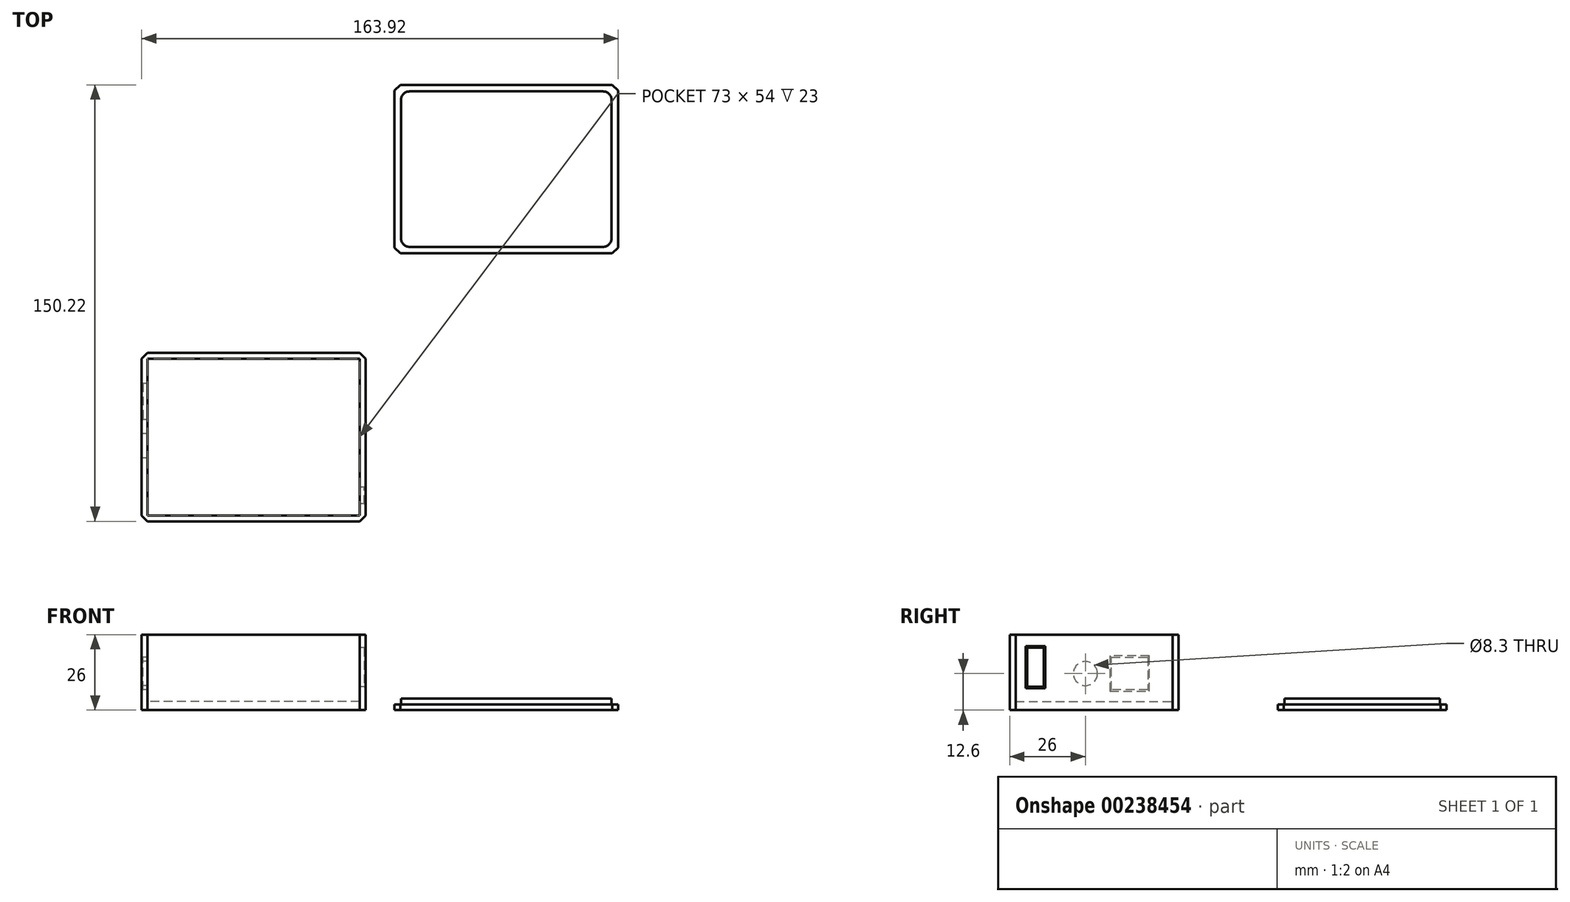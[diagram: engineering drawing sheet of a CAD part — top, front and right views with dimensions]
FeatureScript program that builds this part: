
annotation { "Feature Type Name" : "Feature", "Feature Type Description" : "" }
export const myFeature = defineFeature(function(context is Context, id is Id, definition is map)
    precondition{}
    {
        {
            var Q0;
            Q0=qCreatedBy(makeId("Top.planeOp"),FACE);
            var sketch = newSketch(context, id + "F0", { "sketchPlane" : qUnion([Q0])});
            skLineSegment(sketch, "E0.bottom", {"start": v(38.5, -29) * mm, "end": v(-38.5, -29) * mm});
            skLineSegment(sketch, "E0.top", {"start": v(38.5, 29) * mm, "end": v(-38.5, 29) * mm});
            skLineSegment(sketch, "E0.left", {"start": v(38.5, -29) * mm, "end": v(38.5, 29) * mm});
            skLineSegment(sketch, "E0.right", {"start": v(-38.5, -29) * mm, "end": v(-38.5, 29) * mm});
            skPoint(sketch, "E0.middle", {"position": v(0, 0) * mm});
            skSolve(sketch);
        }
        {
            var Q0;
            Q0 = qSketchRegion(id + "F0", true);
            extrude(context, id + "F1", {"entities" : qUnion([Q0]), "depth" : 3 * mm});
        }
        {
            var Q0;
            Q0=makeQuery(id+"F1.opExtrude","CAP_FACE",FACE,{"disambiguationData":[OSD([sQuery(id+"F0.wireOp",EDGE,"E0.bottom"),sQuery(id+"F0.wireOp",EDGE,"E0.top"),sQuery(id+"F0.wireOp",EDGE,"E0.left"),sQuery(id+"F0.wireOp",EDGE,"E0.right")])],"isStart":false});
            var sketch = newSketch(context, id + "F2", { "sketchPlane" : qUnion([Q0])});
            skLineSegment(sketch, "E1.0", {"start": v(-36.5, -27) * mm, "end": v(-36.5, 27) * mm});
            skLineSegment(sketch, "E1.1", {"start": v(36.5, -27) * mm, "end": v(-36.5, -27) * mm});
            skLineSegment(sketch, "E1.2", {"start": v(36.5, -27) * mm, "end": v(36.5, 27) * mm});
            skLineSegment(sketch, "E1.3", {"start": v(36.5, 27) * mm, "end": v(-36.5, 27) * mm});
            skSolve(sketch);
        }
        {
            var Q0;
            Q0=makeQuery(id+"F2.imprint","IMPRINT",FACE,{"disambiguationData":[TD([[makeQuery(id+"F2.imprint","IMPRINT",EDGE,{"derivedFrom":sQuery(id+"F2.wireOp",EDGE,"E1.0")}),1.0]])]});
            extrude(context, id + "F3", {"entities" : qUnion([Q0]), "operationType" : NewBodyOperationType.ADD, "depth" : 4 * mm});
        }
        {
            var Q0;
            Q0=makeQuery(id+"F3.opExtrude","CAP_FACE",FACE,{"disambiguationData":[OSD([sQuery(id+"F0.wireOp",EDGE,"E0.bottom"),sQuery(id+"F0.wireOp",EDGE,"E0.top"),sQuery(id+"F0.wireOp",EDGE,"E0.left"),sQuery(id+"F0.wireOp",EDGE,"E0.right"),sQuery(id+"F2.wireOp",EDGE,"E1.0"),sQuery(id+"F2.wireOp",EDGE,"E1.1"),sQuery(id+"F2.wireOp",EDGE,"E1.2"),sQuery(id+"F2.wireOp",EDGE,"E1.3")])],"isStart":false});
            var sketch = newSketch(context, id + "F4", { "sketchPlane" : qUnion([Q0])});
            skLineSegment(sketch, "E2", {"start": v(-36.5, 27) * mm, "end": v(-36.5, 18.5) * mm, "construction": true});
            skLineSegment(sketch, "E3", {"start": v(-36.5, 18.5) * mm, "end": v(-38.5, 18.5) * mm});
            skLineSegment(sketch, "E4", {"start": v(-36.5, 6) * mm, "end": v(-38.5, 6) * mm});
            skSolve(sketch);
        }
        {
            var Q0;
            {var subQ2=sQuery(id+"F4.wireOp",EDGE,"E3");Q0=makeQuery(id+"F4.imprint","IMPRINT",FACE,{"disambiguationData":[TD([[makeQuery(id+"F4.imprint","IMPRINT",EDGE,{"derivedFrom":subQ2}),-1.0]])]});}
            extrude(context, id + "F5", {"entities" : qUnion([Q0]), "operationType" : NewBodyOperationType.ADD, "depth" : 19 * mm});
        }
        {
            var Q0;
            Q0=makeQuery(id+"F5.opExtrude","SWEPT_FACE",FACE,{"disambiguationData":[OSD([sQuery(id+"F4.wireOp",EDGE,"E3")])]});
            var sketch = newSketch(context, id + "F6", { "sketchPlane" : qUnion([Q0])});
            skLineSegment(sketch, "E5", {"start": v(-38.5, 18.2) * mm, "end": v(-36.5, 18.2) * mm});
            skSolve(sketch);
        }
        {
            var Q0;
            Q0 = qSketchRegion(id + "F6", true);
            var Q1;
            {var subQ0=sQuery(id+"F6.wireOp",EDGE,"E5");Q1=makeQuery(id+"F6.imprint","IMPRINT",FACE,{"disambiguationData":[TD([[makeQuery(id+"F6.imprint","IMPRINT",EDGE,{"derivedFrom":subQ0}),1.0]])]});}
            extrude(context, id + "F7", {"entities" : qUnion([Q0, Q1]), "operationType" : NewBodyOperationType.ADD, "depth" : 25 * mm});
        }
        {
            var Q0;
            {var subQ0=sQuery(id+"F4.wireOp",EDGE,"E3");var subQ1=sQuery(id+"F0.wireOp",EDGE,"E0.right");var subQ2=makeQuery(id+"F3.opExtrude","CAP_EDGE",EDGE,{"disambiguationData":[OSD([subQ1])],"isStart":false});Q0=makeQuery(id+"F7.boolean.opBoolean","MERGE",FACE,{"derivedFrom":[makeQuery(id+"F5.boolean.opBoolean","MERGE",FACE,{"derivedFrom":[makeQuery(id+"F3.boolean.opBoolean","MERGE",FACE,{"derivedFrom":[makeQuery(id+"F1.opExtrude","SWEPT_FACE",FACE,{"disambiguationData":[OSD([subQ1])]}),makeQuery(id+"F3.opExtrude","SWEPT_FACE",FACE,{"disambiguationData":[OSD([subQ1])]})]}),makeQuery(id+"F5.opExtrude","SWEPT_FACE",FACE,{"disambiguationData":[OSD([subQ1]),TDD([makeQuery(id+"F4.imprint","IMPRINT",EDGE,{"disambiguationData":[TD([[makeQuery(id+"F4.imprint","INTERSECT",VERTEX,{"derivedFrom":[makeQuery(id+"F3.opExtrude","CAP_EDGE",EDGE,{"disambiguationData":[OSD([sQuery(id+"F0.wireOp",EDGE,"E0.bottom")])],"isStart":false}),subQ2]}),-1.0]])],"derivedFrom":subQ2})])]}),makeQuery(id+"F5.opExtrude","SWEPT_FACE",FACE,{"disambiguationData":[OSD([subQ1]),TDD([makeQuery(id+"F4.imprint","IMPRINT",EDGE,{"disambiguationData":[TD([[makeQuery(id+"F4.imprint","INTERSECT",VERTEX,{"derivedFrom":[makeQuery(id+"F3.opExtrude","CAP_EDGE",EDGE,{"disambiguationData":[OSD([sQuery(id+"F0.wireOp",EDGE,"E0.top")])],"isStart":false}),subQ2]}),1.0]])],"derivedFrom":subQ2})])]})]}),makeQuery(id+"F7.opExtrude","SWEPT_FACE",FACE,{"disambiguationData":[OSD([subQ1,subQ0])]})]});}
            var sketch = newSketch(context, id + "F8", { "sketchPlane" : qUnion([Q0])});
            skLineSegment(sketch, "E6", {"start": v(-6, 12.6) * mm, "end": v(3, 12.6) * mm, "construction": true});
            skPoint(sketch, "E7", {"position": v(3, 12.6) * mm});
            skSolve(sketch);
        }
        {
            var Q0;
            Q0=sQuery(id+"F8.wireOp",VERTEX,"E7");
            var Q1;
            Q1=makeQuery(id+"F1.opExtrude","SWEPT_BODY",BODY,{"disambiguationData":[OSD([sQuery(id+"F0.wireOp",EDGE,"E0.bottom"),sQuery(id+"F0.wireOp",EDGE,"E0.top"),sQuery(id+"F0.wireOp",EDGE,"E0.left"),sQuery(id+"F0.wireOp",EDGE,"E0.right")])]});
            hole(context, id + "F9", {"style" : HoleStyle.SIMPLE, "endStyle" : HoleEndStyle.BLIND, "holeDiameter" : 8.3 * mm, "holeDepth" : 10 * mm, "locations" : qUnion([Q0]), "scope" : qUnion([Q1])});
        }
        {
            var Q0;
            {var subQ0=sQuery(id+"F2.wireOp",EDGE,"E1.2");Q0=makeQuery(id+"F5.boolean.opBoolean","MERGE",FACE,{"derivedFrom":[makeQuery(id+"F3.opExtrude","SWEPT_FACE",FACE,{"disambiguationData":[OSD([subQ0])]}),makeQuery(id+"F5.opExtrude","SWEPT_FACE",FACE,{"disambiguationData":[OSD([subQ0])]})]});}
            var sketch = newSketch(context, id + "F10", { "sketchPlane" : qUnion([Q0])});
            skLineSegment(sketch, "E8", {"start": v(23, 3) * mm, "end": v(23, 8) * mm, "construction": true});
            skLineSegment(sketch, "E9", {"start": v(23, 8) * mm, "end": v(27, 8) * mm});
            skLineSegment(sketch, "E10.bottom", {"start": v(23, 8) * mm, "end": v(17.3, 8) * mm});
            skLineSegment(sketch, "E10.top", {"start": v(23, 21.5) * mm, "end": v(17.3, 21.5) * mm});
            skLineSegment(sketch, "E10.left", {"start": v(23, 8) * mm, "end": v(23, 21.5) * mm});
            skLineSegment(sketch, "E10.right", {"start": v(17.3, 8) * mm, "end": v(17.3, 21.5) * mm});
            skSolve(sketch);
        }
        {
            var Q0;
            Q0 = qSketchRegion(id + "F10", true);
            extrude(context, id + "F11", {"entities" : qUnion([Q0]), "operationType" : NewBodyOperationType.REMOVE, "oppositeDirection" : true, "depth" : 25 * mm});
        }
        {
            var Q0;
            {var subQ0=sQuery(id+"F0.wireOp",EDGE,"E0.right");var subQ1=sQuery(id+"F0.wireOp",EDGE,"E0.bottom");Q0=makeQuery(id+"F5.boolean.opBoolean","MERGE",EDGE,{"derivedFrom":[makeQuery(id+"F3.boolean.opBoolean","MERGE",EDGE,{"derivedFrom":[makeQuery(id+"F1.opExtrude","SWEPT_EDGE",EDGE,{"disambiguationData":[OSD([subQ1,subQ0])]}),makeQuery(id+"F3.opExtrude","SWEPT_EDGE",EDGE,{"disambiguationData":[OSD([subQ1,subQ0])]})]}),makeQuery(id+"F5.opExtrude","SWEPT_EDGE",EDGE,{"disambiguationData":[OSD([subQ1,subQ0])]})]});}
            var Q1;
            {var subQ0=sQuery(id+"F0.wireOp",EDGE,"E0.left");var subQ1=sQuery(id+"F0.wireOp",EDGE,"E0.bottom");Q1=makeQuery(id+"F5.boolean.opBoolean","MERGE",EDGE,{"derivedFrom":[makeQuery(id+"F3.boolean.opBoolean","MERGE",EDGE,{"derivedFrom":[makeQuery(id+"F1.opExtrude","SWEPT_EDGE",EDGE,{"disambiguationData":[OSD([subQ1,subQ0])]}),makeQuery(id+"F3.opExtrude","SWEPT_EDGE",EDGE,{"disambiguationData":[OSD([subQ1,subQ0])]})]}),makeQuery(id+"F5.opExtrude","SWEPT_EDGE",EDGE,{"disambiguationData":[OSD([subQ1,subQ0])]})]});}
            var Q2;
            {var subQ0=sQuery(id+"F0.wireOp",EDGE,"E0.left");var subQ1=sQuery(id+"F0.wireOp",EDGE,"E0.top");Q2=makeQuery(id+"F5.boolean.opBoolean","MERGE",EDGE,{"derivedFrom":[makeQuery(id+"F3.boolean.opBoolean","MERGE",EDGE,{"derivedFrom":[makeQuery(id+"F1.opExtrude","SWEPT_EDGE",EDGE,{"disambiguationData":[OSD([subQ1,subQ0])]}),makeQuery(id+"F3.opExtrude","SWEPT_EDGE",EDGE,{"disambiguationData":[OSD([subQ1,subQ0])]})]}),makeQuery(id+"F5.opExtrude","SWEPT_EDGE",EDGE,{"disambiguationData":[OSD([subQ1,subQ0])]})]});}
            var Q3;
            {var subQ0=sQuery(id+"F0.wireOp",EDGE,"E0.right");var subQ1=sQuery(id+"F0.wireOp",EDGE,"E0.top");Q3=makeQuery(id+"F5.boolean.opBoolean","MERGE",EDGE,{"derivedFrom":[makeQuery(id+"F3.boolean.opBoolean","MERGE",EDGE,{"derivedFrom":[makeQuery(id+"F1.opExtrude","SWEPT_EDGE",EDGE,{"disambiguationData":[OSD([subQ1,subQ0])]}),makeQuery(id+"F3.opExtrude","SWEPT_EDGE",EDGE,{"disambiguationData":[OSD([subQ1,subQ0])]})]}),makeQuery(id+"F5.opExtrude","SWEPT_EDGE",EDGE,{"disambiguationData":[OSD([subQ1,subQ0])]})]});}
            chamfer(context, id + "F12", {"entities" : qUnion([Q0, Q1, Q2, Q3]), "width" : 2 * mm, "tangentPropagation" : true});
        }
        {
            var Q0;
            {var subQ0=sQuery(id+"F0.wireOp",EDGE,"E0.left");Q0=makeQuery(id+"F11.boolean.opBoolean","INTERSECT",EDGE,{"derivedFrom":[makeQuery(id+"F5.boolean.opBoolean","MERGE",FACE,{"derivedFrom":[makeQuery(id+"F3.boolean.opBoolean","MERGE",FACE,{"derivedFrom":[makeQuery(id+"F1.opExtrude","SWEPT_FACE",FACE,{"disambiguationData":[OSD([subQ0])]}),makeQuery(id+"F3.opExtrude","SWEPT_FACE",FACE,{"disambiguationData":[OSD([subQ0])]})]}),makeQuery(id+"F5.opExtrude","SWEPT_FACE",FACE,{"disambiguationData":[OSD([subQ0])]})]}),makeQuery(id+"F11.opExtrude","SWEPT_FACE",FACE,{"disambiguationData":[OSD([sQuery(id+"F10.wireOp",EDGE,"E10.right")])]})]});}
            var Q1;
            {var subQ0=sQuery(id+"F0.wireOp",EDGE,"E0.left");Q1=makeQuery(id+"F11.boolean.opBoolean","INTERSECT",EDGE,{"derivedFrom":[makeQuery(id+"F5.boolean.opBoolean","MERGE",FACE,{"derivedFrom":[makeQuery(id+"F3.boolean.opBoolean","MERGE",FACE,{"derivedFrom":[makeQuery(id+"F1.opExtrude","SWEPT_FACE",FACE,{"disambiguationData":[OSD([subQ0])]}),makeQuery(id+"F3.opExtrude","SWEPT_FACE",FACE,{"disambiguationData":[OSD([subQ0])]})]}),makeQuery(id+"F5.opExtrude","SWEPT_FACE",FACE,{"disambiguationData":[OSD([subQ0])]})]}),makeQuery(id+"F11.opExtrude","SWEPT_FACE",FACE,{"disambiguationData":[OSD([sQuery(id+"F10.wireOp",EDGE,"E10.top")])]})]});}
            var Q2;
            {var subQ0=sQuery(id+"F0.wireOp",EDGE,"E0.left");Q2=makeQuery(id+"F11.boolean.opBoolean","INTERSECT",EDGE,{"derivedFrom":[makeQuery(id+"F5.boolean.opBoolean","MERGE",FACE,{"derivedFrom":[makeQuery(id+"F3.boolean.opBoolean","MERGE",FACE,{"derivedFrom":[makeQuery(id+"F1.opExtrude","SWEPT_FACE",FACE,{"disambiguationData":[OSD([subQ0])]}),makeQuery(id+"F3.opExtrude","SWEPT_FACE",FACE,{"disambiguationData":[OSD([subQ0])]})]}),makeQuery(id+"F5.opExtrude","SWEPT_FACE",FACE,{"disambiguationData":[OSD([subQ0])]})]}),makeQuery(id+"F11.opExtrude","SWEPT_FACE",FACE,{"disambiguationData":[OSD([sQuery(id+"F10.wireOp",EDGE,"E10.left")])]})]});}
            var Q3;
            {var subQ0=sQuery(id+"F0.wireOp",EDGE,"E0.left");Q3=makeQuery(id+"F11.boolean.opBoolean","INTERSECT",EDGE,{"derivedFrom":[makeQuery(id+"F5.boolean.opBoolean","MERGE",FACE,{"derivedFrom":[makeQuery(id+"F3.boolean.opBoolean","MERGE",FACE,{"derivedFrom":[makeQuery(id+"F1.opExtrude","SWEPT_FACE",FACE,{"disambiguationData":[OSD([subQ0])]}),makeQuery(id+"F3.opExtrude","SWEPT_FACE",FACE,{"disambiguationData":[OSD([subQ0])]})]}),makeQuery(id+"F5.opExtrude","SWEPT_FACE",FACE,{"disambiguationData":[OSD([subQ0])]})]}),makeQuery(id+"F11.opExtrude","SWEPT_FACE",FACE,{"disambiguationData":[OSD([sQuery(id+"F10.wireOp",EDGE,"E10.bottom")])]})]});}
            chamfer(context, id + "F13", {"entities" : qUnion([Q0, Q1, Q2, Q3]), "width" : .5 * mm, "tangentPropagation" : true});
        }
        {
            var Q0;
            Q0=makeQuery(id+"F5.opExtrude","SWEPT_EDGE",EDGE,{"disambiguationData":[OSD([sQuery(id+"F0.wireOp",EDGE,"E0.right"),sQuery(id+"F4.wireOp",EDGE,"E3")])]});
            var Q1;
            Q1=makeQuery(id+"F7.opExtrude","SWEPT_EDGE",EDGE,{"disambiguationData":[OSD([sQuery(id+"F0.wireOp",EDGE,"E0.right"),sQuery(id+"F4.wireOp",EDGE,"E3"),sQuery(id+"F6.wireOp",EDGE,"E5")])]});
            var Q2;
            Q2=makeQuery(id+"F5.opExtrude","SWEPT_EDGE",EDGE,{"disambiguationData":[OSD([sQuery(id+"F0.wireOp",EDGE,"E0.right"),sQuery(id+"F4.wireOp",EDGE,"E4")])]});
            var Q3;
            Q3=makeQuery(id+"F3.opExtrude","CAP_EDGE",EDGE,{"disambiguationData":[OSD([sQuery(id+"F0.wireOp",EDGE,"E0.right")])],"isStart":false});
            chamfer(context, id + "F14", {"entities" : qUnion([Q0, Q1, Q2, Q3]), "width" : .5 * mm, "tangentPropagation" : true});
        }
        {
            var Q0;
            Q0=qCreatedBy(makeId("Top.planeOp"),FACE);
            var sketch = newSketch(context, id + "F15", { "sketchPlane" : qUnion([Q0])});
            skLineSegment(sketch, "E11.bottom", {"start": v(48.42, 63.22) * mm, "end": v(125.42, 63.22) * mm});
            skLineSegment(sketch, "E11.top", {"start": v(48.42, 121.22) * mm, "end": v(125.42, 121.22) * mm});
            skLineSegment(sketch, "E11.left", {"start": v(48.42, 63.22) * mm, "end": v(48.42, 121.22) * mm});
            skLineSegment(sketch, "E11.right", {"start": v(125.42, 63.22) * mm, "end": v(125.42, 121.22) * mm});
            skSolve(sketch);
        }
        {
            var Q0;
            Q0 = qSketchRegion(id + "F15", true);
            extrude(context, id + "F16", {"entities" : qUnion([Q0]), "depth" : 2 * mm});
        }
        {
            var Q0;
            Q0=makeQuery(id+"F16.opExtrude","CAP_FACE",FACE,{"disambiguationData":[OSD([sQuery(id+"F15.wireOp",EDGE,"E11.bottom"),sQuery(id+"F15.wireOp",EDGE,"E11.top"),sQuery(id+"F15.wireOp",EDGE,"E11.left"),sQuery(id+"F15.wireOp",EDGE,"E11.right")])],"isStart":false});
            var sketch = newSketch(context, id + "F17", { "sketchPlane" : qUnion([Q0])});
            skLineSegment(sketch, "E12.0", {"start": v(50.67, 118.97) * mm, "end": v(123.17, 118.97) * mm});
            skLineSegment(sketch, "E12.1", {"start": v(50.67, 65.47) * mm, "end": v(50.67, 118.97) * mm});
            skLineSegment(sketch, "E12.2", {"start": v(50.67, 65.47) * mm, "end": v(123.17, 65.47) * mm});
            skLineSegment(sketch, "E12.3", {"start": v(123.17, 65.47) * mm, "end": v(123.17, 118.97) * mm});
            skSolve(sketch);
        }
        {
            var Q0;
            Q0 = qSketchRegion(id + "F17", true);
            extrude(context, id + "F18", {"entities" : qUnion([Q0]), "operationType" : NewBodyOperationType.ADD, "depth" : 2 * mm});
        }
        {
            var Q0;
            Q0=makeQuery(id+"F18.opExtrude","SWEPT_EDGE",EDGE,{"disambiguationData":[OSD([sQuery(id+"F17.wireOp",EDGE,"E12.2"),sQuery(id+"F17.wireOp",EDGE,"E12.3")])]});
            var Q1;
            Q1=makeQuery(id+"F18.opExtrude","SWEPT_EDGE",EDGE,{"disambiguationData":[OSD([sQuery(id+"F17.wireOp",EDGE,"E12.1"),sQuery(id+"F17.wireOp",EDGE,"E12.2")])]});
            var Q2;
            Q2=makeQuery(id+"F18.opExtrude","SWEPT_EDGE",EDGE,{"disambiguationData":[OSD([sQuery(id+"F17.wireOp",EDGE,"E12.0"),sQuery(id+"F17.wireOp",EDGE,"E12.1")])]});
            var Q3;
            Q3=makeQuery(id+"F18.opExtrude","SWEPT_EDGE",EDGE,{"disambiguationData":[OSD([sQuery(id+"F17.wireOp",EDGE,"E12.0"),sQuery(id+"F17.wireOp",EDGE,"E12.3")])]});
            fillet(context, id + "F19", {"entities" : qUnion([Q0, Q1, Q2, Q3]), "radius" : 3 * mm, "tangentPropagation" : true, "allowEdgeOverflow" : false});
        }
        {
            var Q0;
            Q0=makeQuery(id+"F16.opExtrude","SWEPT_EDGE",EDGE,{"disambiguationData":[OSD([sQuery(id+"F15.wireOp",EDGE,"E11.top"),sQuery(id+"F15.wireOp",EDGE,"E11.left")])]});
            var Q1;
            Q1=makeQuery(id+"F16.opExtrude","SWEPT_EDGE",EDGE,{"disambiguationData":[OSD([sQuery(id+"F15.wireOp",EDGE,"E11.top"),sQuery(id+"F15.wireOp",EDGE,"E11.right")])]});
            var Q2;
            Q2=makeQuery(id+"F16.opExtrude","SWEPT_EDGE",EDGE,{"disambiguationData":[OSD([sQuery(id+"F15.wireOp",EDGE,"E11.bottom"),sQuery(id+"F15.wireOp",EDGE,"E11.right")])]});
            var Q3;
            Q3=makeQuery(id+"F16.opExtrude","SWEPT_EDGE",EDGE,{"disambiguationData":[OSD([sQuery(id+"F15.wireOp",EDGE,"E11.bottom"),sQuery(id+"F15.wireOp",EDGE,"E11.left")])]});
            chamfer(context, id + "F20", {"entities" : qUnion([Q0, Q1, Q2, Q3]), "width" : 2 * mm, "tangentPropagation" : true});
        }
    });
